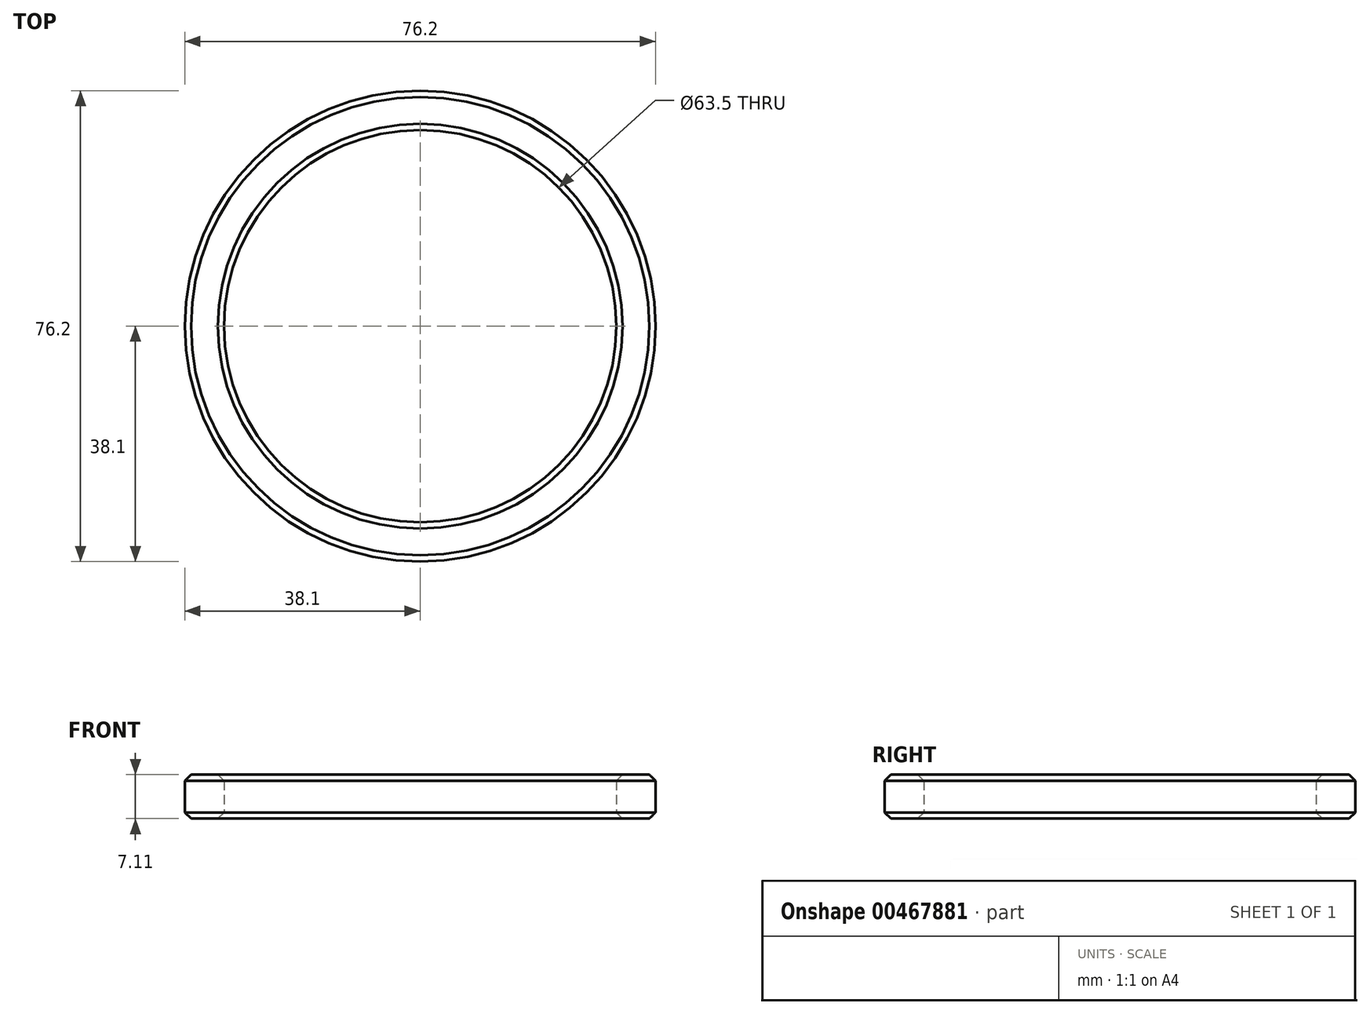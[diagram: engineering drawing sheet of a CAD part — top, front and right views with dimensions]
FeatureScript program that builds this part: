
annotation { "Feature Type Name" : "Feature", "Feature Type Description" : "" }
export const myFeature = defineFeature(function(context is Context, id is Id, definition is map)
    precondition{}
    {
        {
            var Q0;
            Q0=qCreatedBy(makeId("Top.planeOp"),FACE);
            var sketch = newSketch(context, id + "F0", { "sketchPlane" : qUnion([Q0])});
            skCircle(sketch, "E0", {"center": v(0, 0) * mm, "radius": 38.1 * mm});
            skCircle(sketch, "E1", {"center": v(0, 0) * mm, "radius": 31.75 * mm});
            skSolve(sketch);
        }
        {
            var Q0;
            Q0 = qSketchRegion(id + "F0", true);
            extrude(context, id + "F1", {"entities" : qUnion([Q0]), "depth" : 7.11 * mm});
        }
        {
            var Q0;
            Q0=makeQuery(id+"F1.opExtrude","CAP_EDGE",EDGE,{"disambiguationData":[OSD([sQuery(id+"F0.wireOp",EDGE,"E0")])],"isStart":true});
            var Q1;
            Q1=makeQuery(id+"F1.opExtrude","CAP_EDGE",EDGE,{"disambiguationData":[OSD([sQuery(id+"F0.wireOp",EDGE,"E0")])],"isStart":false});
            var Q2;
            Q2=makeQuery(id+"F1.opExtrude","CAP_EDGE",EDGE,{"disambiguationData":[OSD([sQuery(id+"F0.wireOp",EDGE,"E1")])],"isStart":false});
            var Q3;
            Q3=makeQuery(id+"F1.opExtrude","CAP_EDGE",EDGE,{"disambiguationData":[OSD([sQuery(id+"F0.wireOp",EDGE,"E1")])],"isStart":true});
            chamfer(context, id + "F2", {"entities" : qUnion([Q0, Q1, Q2, Q3]), "width" : 1 * mm, "tangentPropagation" : true});
        }
    });
